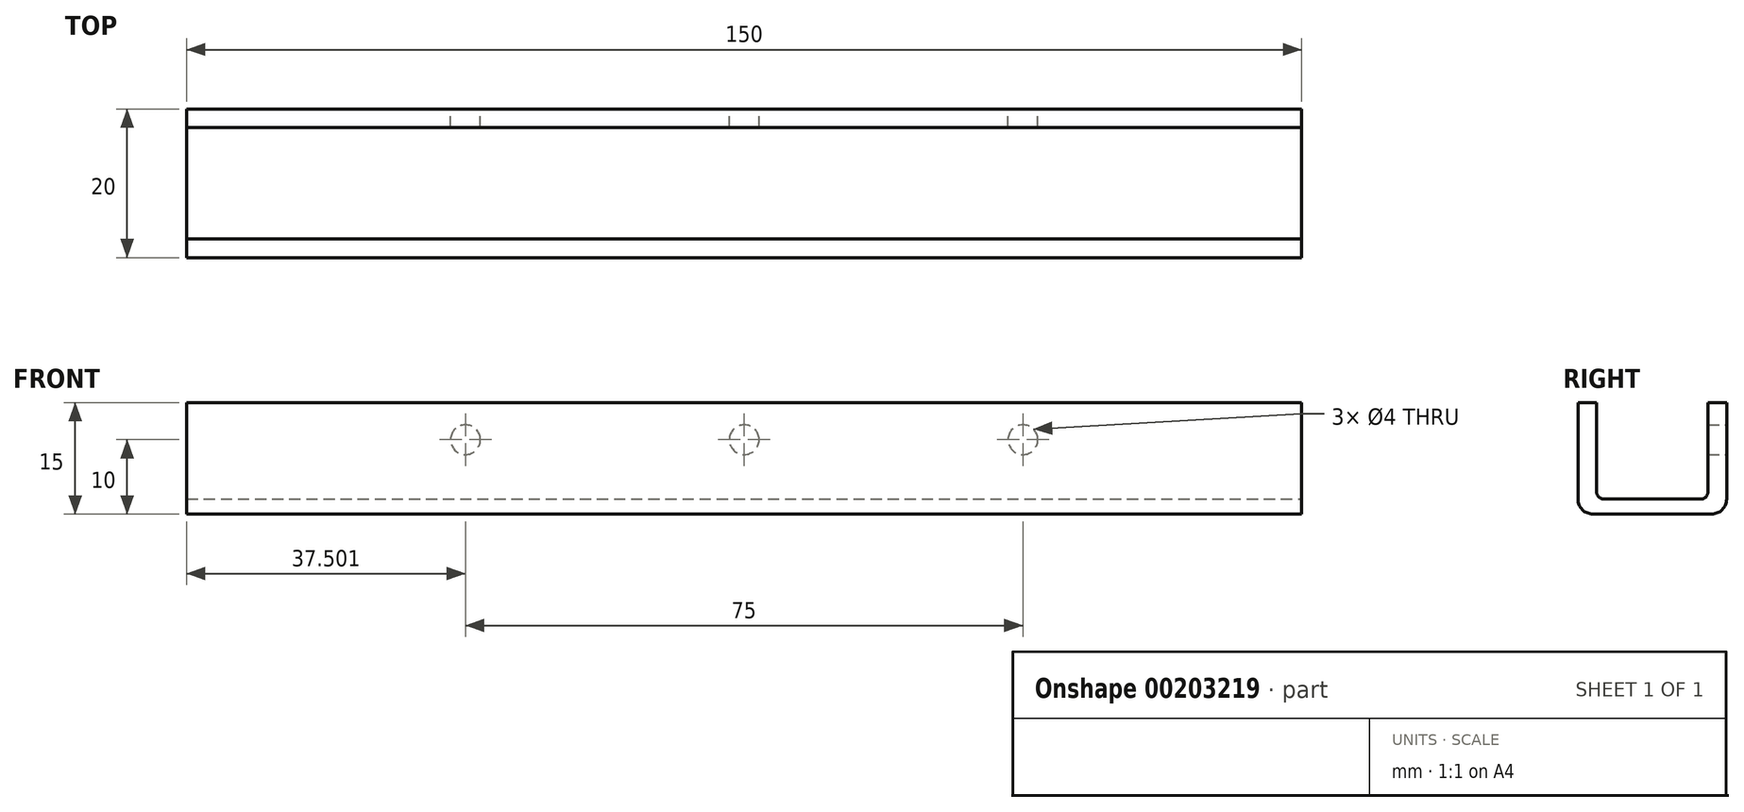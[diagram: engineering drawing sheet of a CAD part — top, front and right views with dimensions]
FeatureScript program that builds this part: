
annotation { "Feature Type Name" : "Feature", "Feature Type Description" : "" }
export const myFeature = defineFeature(function(context is Context, id is Id, definition is map)
    precondition{}
    {
        {
            var Q0;
            Q0=qCreatedBy(makeId("Top.planeOp"),FACE);
            var sketch = newSketch(context, id + "F0", { "sketchPlane" : qUnion([Q0])});
            skLineSegment(sketch, "E0.bottom", {"start": v(-73.62, 3.95) * mm, "end": v(76.38, 3.95) * mm});
            skLineSegment(sketch, "E0.top", {"start": v(-73.62, -16.05) * mm, "end": v(76.38, -16.05) * mm});
            skLineSegment(sketch, "E0.left", {"start": v(-73.62, 3.95) * mm, "end": v(-73.62, -16.05) * mm});
            skLineSegment(sketch, "E0.right", {"start": v(76.38, 3.95) * mm, "end": v(76.38, -16.05) * mm});
            skSolve(sketch);
        }
        {
            var Q0;
            Q0=makeQuery(id+"F0.imprint","IMPRINT",FACE,{"disambiguationData":[TD([[makeQuery(id+"F0.imprint","IMPRINT",EDGE,{"derivedFrom":sQuery(id+"F0.wireOp",EDGE,"E0.bottom")}),-1.0]])]});
            extrude(context, id + "F1", {"entities" : qUnion([Q0]), "depth" : 15 * mm});
        }
        {
            var Q0;
            Q0=makeQuery(id+"F1.opExtrude","CAP_FACE",FACE,{"disambiguationData":[OSD([sQuery(id+"F0.wireOp",EDGE,"E0.bottom"),sQuery(id+"F0.wireOp",EDGE,"E0.top"),sQuery(id+"F0.wireOp",EDGE,"E0.left"),sQuery(id+"F0.wireOp",EDGE,"E0.right")])],"isStart":false});
            var sketch = newSketch(context, id + "F2", { "sketchPlane" : qUnion([Q0])});
            skLineSegment(sketch, "E1.bottom", {"start": v(-73.62, 1.45) * mm, "end": v(76.38, 1.45) * mm});
            skLineSegment(sketch, "E1.top", {"start": v(-73.62, -13.55) * mm, "end": v(76.38, -13.55) * mm});
            skLineSegment(sketch, "E1.left", {"start": v(-73.62, 1.45) * mm, "end": v(-73.62, -13.55) * mm});
            skLineSegment(sketch, "E1.right", {"start": v(76.38, 1.45) * mm, "end": v(76.38, -13.55) * mm});
            skSolve(sketch);
        }
        {
            var Q0;
            Q0=makeQuery(id+"F2.imprint","IMPRINT",FACE,{"disambiguationData":[TD([[makeQuery(id+"F2.imprint","IMPRINT",EDGE,{"derivedFrom":sQuery(id+"F2.wireOp",EDGE,"E1.bottom")}),-1.0]])]});
            extrude(context, id + "F3", {"entities" : qUnion([Q0]), "operationType" : NewBodyOperationType.REMOVE, "oppositeDirection" : true, "depth" : 13 * mm});
        }
        {
            var Q0;
            Q0=makeQuery(id+"F1.opExtrude","SWEPT_FACE",FACE,{"disambiguationData":[OSD([sQuery(id+"F0.wireOp",EDGE,"E0.bottom")])]});
            var sketch = newSketch(context, id + "F4", { "sketchPlane" : qUnion([Q0])});
            skCircle(sketch, "E2", {"center": v(-38.88, 10) * mm, "radius": 2 * mm});
            skCircle(sketch, "E3", {"center": v(-1.38, 10) * mm, "radius": 2 * mm});
            skCircle(sketch, "E4", {"center": v(36.12, 10) * mm, "radius": 2 * mm});
            skSolve(sketch);
        }
        {
            var Q0;
            Q0=makeQuery(id+"F4.imprint","IMPRINT",FACE,{"disambiguationData":[TD([[makeQuery(id+"F4.imprint","IMPRINT",EDGE,{"derivedFrom":sQuery(id+"F4.wireOp",EDGE,"E2")}),1.0]])]});
            var Q1;
            Q1=makeQuery(id+"F4.imprint","IMPRINT",FACE,{"disambiguationData":[TD([[makeQuery(id+"F4.imprint","IMPRINT",EDGE,{"derivedFrom":sQuery(id+"F4.wireOp",EDGE,"E3")}),1.0]])]});
            var Q2;
            Q2=makeQuery(id+"F4.imprint","IMPRINT",FACE,{"disambiguationData":[TD([[makeQuery(id+"F4.imprint","IMPRINT",EDGE,{"derivedFrom":sQuery(id+"F4.wireOp",EDGE,"E4")}),1.0]])]});
            extrude(context, id + "F5", {"entities" : qUnion([Q0, Q1, Q2]), "operationType" : NewBodyOperationType.REMOVE, "oppositeDirection" : true, "depth" : 2.5 * mm});
        }
        {
            var Q0;
            Q0=makeQuery(id+"F1.opExtrude","CAP_EDGE",EDGE,{"disambiguationData":[OSD([sQuery(id+"F0.wireOp",EDGE,"E0.top")])],"isStart":true});
            var Q1;
            Q1=makeQuery(id+"F1.opExtrude","CAP_EDGE",EDGE,{"disambiguationData":[OSD([sQuery(id+"F0.wireOp",EDGE,"E0.bottom")])],"isStart":true});
            fillet(context, id + "F6", {"entities" : qUnion([Q0, Q1]), "radius" : 2 * mm, "tangentPropagation" : true, "allowEdgeOverflow" : false});
        }
        {
            var Q0;
            Q0=makeQuery(id+"F3.boolean.opBoolean","COPY",EDGE,{"derivedFrom":makeQuery(id+"F3.opExtrude","CAP_EDGE",EDGE,{"disambiguationData":[OSD([sQuery(id+"F2.wireOp",EDGE,"E1.top")])],"isStart":false})});
            var Q1;
            Q1=makeQuery(id+"F3.boolean.opBoolean","COPY",EDGE,{"derivedFrom":makeQuery(id+"F3.opExtrude","CAP_EDGE",EDGE,{"disambiguationData":[OSD([sQuery(id+"F2.wireOp",EDGE,"E1.bottom")])],"isStart":false})});
            fillet(context, id + "F7", {"entities" : qUnion([Q0, Q1]), "radius" : 1 * mm, "tangentPropagation" : true, "allowEdgeOverflow" : false});
        }
    });
